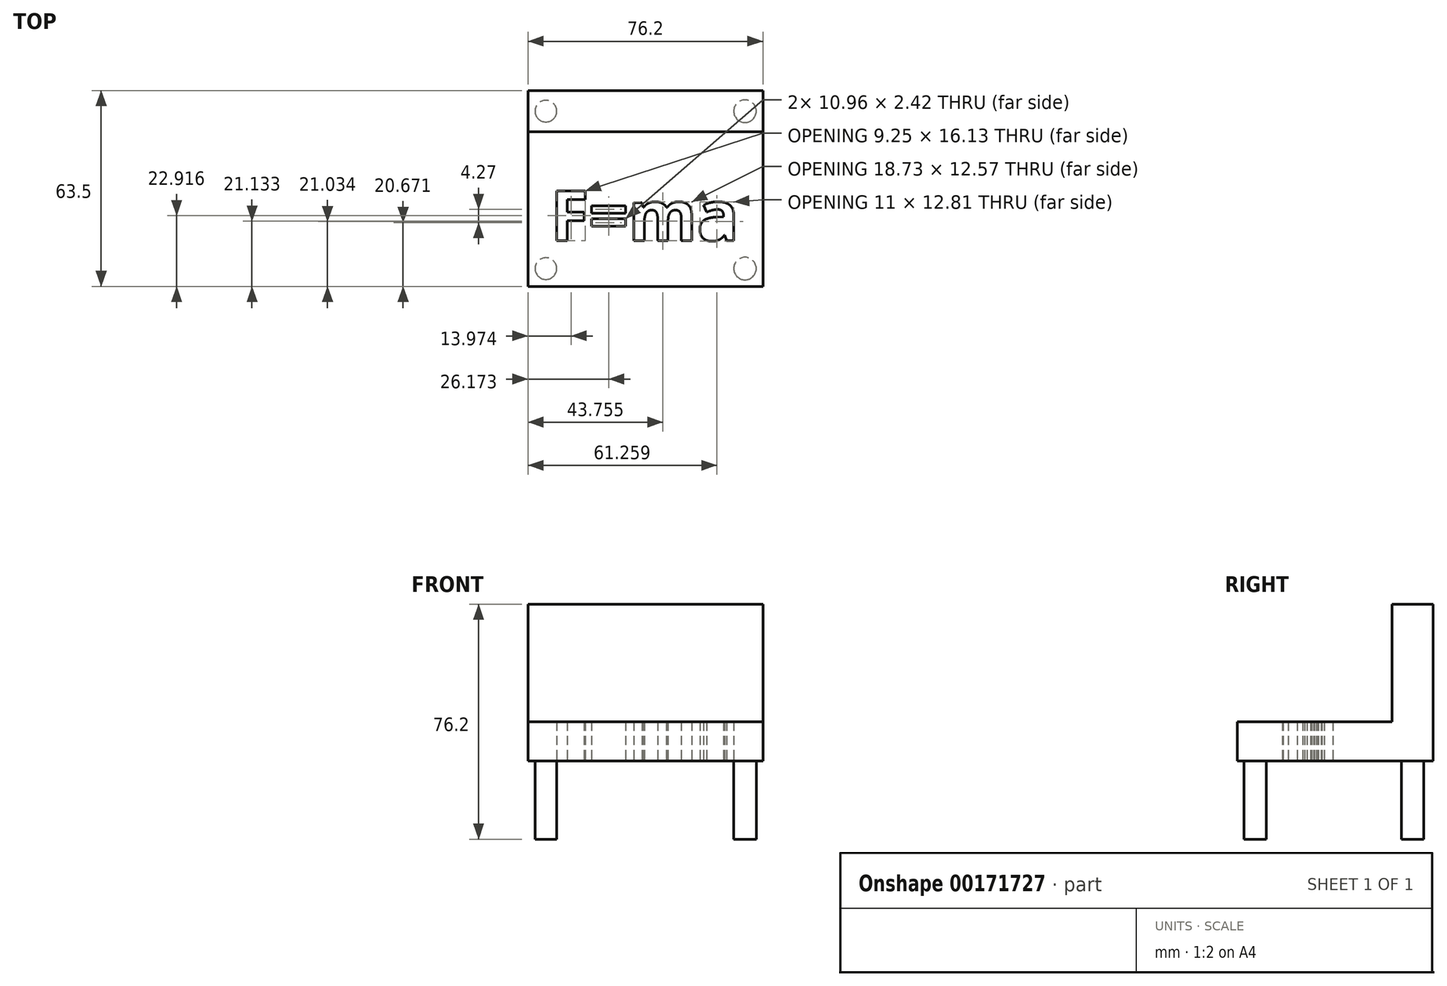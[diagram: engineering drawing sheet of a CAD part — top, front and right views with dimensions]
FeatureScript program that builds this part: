
annotation { "Feature Type Name" : "Feature", "Feature Type Description" : "" }
export const myFeature = defineFeature(function(context is Context, id is Id, definition is map)
    precondition{}
    {
        {
            var Q0;
            Q0=qCreatedBy(makeId("Top.planeOp"),FACE);
            var sketch = newSketch(context, id + "F0", { "sketchPlane" : qUnion([Q0])});
            skLineSegment(sketch, "E0.bottom", {"start": v(-23.67, 32.38) * mm, "end": v(52.53, 32.38) * mm});
            skLineSegment(sketch, "E0.top", {"start": v(-23.67, -31.12) * mm, "end": v(52.53, -31.12) * mm});
            skLineSegment(sketch, "E0.left", {"start": v(-23.67, 32.38) * mm, "end": v(-23.67, -31.12) * mm});
            skLineSegment(sketch, "E0.right", {"start": v(52.53, 32.38) * mm, "end": v(52.53, -31.12) * mm});
            skText(sketch, "E1", { "text": "F=ma", "fontName": "OpenSans-Bold.ttf"});
            const initialGuessF0  = {"E1": [-0.01635, -0.01627, 1, 0, 0.01627]};
            skSetInitialGuess(sketch, initialGuessF0);
            skSolve(sketch);
        }
        {
            var Q0;
            Q0 = qSketchRegion(id + "F0", true);
            extrude(context, id + "F1", {"entities" : qUnion([Q0]), "depth" : 12.7 * mm});
        }
        {
            var Q0;
            Q0=makeQuery(id+"F1.opExtrude","CAP_FACE",FACE,{"disambiguationData":[OSD([sQuery(id+"F0.wireOp",EDGE,"E0.bottom"),sQuery(id+"F0.wireOp",EDGE,"E0.top"),sQuery(id+"F0.wireOp",EDGE,"E0.left"),sQuery(id+"F0.wireOp",EDGE,"E0.right"),sQuery(id+"F0.wireOp",EDGE,"E1.sketch_text.stroke-0"),sQuery(id+"F0.wireOp",EDGE,"E1.sketch_text.stroke-1"),sQuery(id+"F0.wireOp",EDGE,"E1.sketch_text.stroke-2"),sQuery(id+"F0.wireOp",EDGE,"E1.sketch_text.stroke-3"),sQuery(id+"F0.wireOp",EDGE,"E1.sketch_text.stroke-4"),sQuery(id+"F0.wireOp",EDGE,"E1.sketch_text.stroke-5"),sQuery(id+"F0.wireOp",EDGE,"E1.sketch_text.stroke-6"),sQuery(id+"F0.wireOp",EDGE,"E1.sketch_text.stroke-7"),sQuery(id+"F0.wireOp",EDGE,"E1.sketch_text.stroke-8"),sQuery(id+"F0.wireOp",EDGE,"E1.sketch_text.stroke-9"),sQuery(id+"F0.wireOp",EDGE,"E1.sketch_text.stroke-10"),sQuery(id+"F0.wireOp",EDGE,"E1.sketch_text.stroke-11"),sQuery(id+"F0.wireOp",EDGE,"E1.sketch_text.stroke-12"),sQuery(id+"F0.wireOp",EDGE,"E1.sketch_text.stroke-13"),sQuery(id+"F0.wireOp",EDGE,"E1.sketch_text.stroke-14"),sQuery(id+"F0.wireOp",EDGE,"E1.sketch_text.stroke-15"),sQuery(id+"F0.wireOp",EDGE,"E1.sketch_text.stroke-16"),sQuery(id+"F0.wireOp",EDGE,"E1.sketch_text.stroke-17"),sQuery(id+"F0.wireOp",EDGE,"E1.sketch_text.stroke-18"),sQuery(id+"F0.wireOp",EDGE,"E1.sketch_text.stroke-19"),sQuery(id+"F0.wireOp",EDGE,"E1.sketch_text.stroke-20"),sQuery(id+"F0.wireOp",EDGE,"E1.sketch_text.stroke-21"),sQuery(id+"F0.wireOp",EDGE,"E1.sketch_text.stroke-22"),sQuery(id+"F0.wireOp",EDGE,"E1.sketch_text.stroke-23"),sQuery(id+"F0.wireOp",EDGE,"E1.sketch_text.stroke-24"),sQuery(id+"F0.wireOp",EDGE,"E1.sketch_text.stroke-25"),sQuery(id+"F0.wireOp",EDGE,"E1.sketch_text.stroke-26"),sQuery(id+"F0.wireOp",EDGE,"E1.sketch_text.stroke-27"),sQuery(id+"F0.wireOp",EDGE,"E1.sketch_text.stroke-28"),sQuery(id+"F0.wireOp",EDGE,"E1.sketch_text.stroke-29"),sQuery(id+"F0.wireOp",EDGE,"E1.sketch_text.stroke-30"),sQuery(id+"F0.wireOp",EDGE,"E1.sketch_text.stroke-31"),sQuery(id+"F0.wireOp",EDGE,"E1.sketch_text.stroke-32"),sQuery(id+"F0.wireOp",EDGE,"E1.sketch_text.stroke-33"),sQuery(id+"F0.wireOp",EDGE,"E1.sketch_text.stroke-34"),sQuery(id+"F0.wireOp",EDGE,"E1.sketch_text.stroke-35"),sQuery(id+"F0.wireOp",EDGE,"E1.sketch_text.stroke-36"),sQuery(id+"F0.wireOp",EDGE,"E1.sketch_text.stroke-37"),sQuery(id+"F0.wireOp",EDGE,"E1.sketch_text.stroke-38"),sQuery(id+"F0.wireOp",EDGE,"E1.sketch_text.stroke-39"),sQuery(id+"F0.wireOp",EDGE,"E1.sketch_text.stroke-40"),sQuery(id+"F0.wireOp",EDGE,"E1.sketch_text.stroke-41"),sQuery(id+"F0.wireOp",EDGE,"E1.sketch_text.stroke-42"),sQuery(id+"F0.wireOp",EDGE,"E1.sketch_text.stroke-43"),sQuery(id+"F0.wireOp",EDGE,"E1.sketch_text.stroke-44"),sQuery(id+"F0.wireOp",EDGE,"E1.sketch_text.stroke-45"),sQuery(id+"F0.wireOp",EDGE,"E1.sketch_text.stroke-46"),sQuery(id+"F0.wireOp",EDGE,"E1.sketch_text.stroke-47"),sQuery(id+"F0.wireOp",EDGE,"E1.sketch_text.stroke-48"),sQuery(id+"F0.wireOp",EDGE,"E1.sketch_text.stroke-49"),sQuery(id+"F0.wireOp",EDGE,"E1.sketch_text.stroke-50"),sQuery(id+"F0.wireOp",EDGE,"E1.sketch_text.stroke-51"),sQuery(id+"F0.wireOp",EDGE,"E1.sketch_text.stroke-52"),sQuery(id+"F0.wireOp",EDGE,"E1.sketch_text.stroke-53"),sQuery(id+"F0.wireOp",EDGE,"E1.sketch_text.stroke-54"),sQuery(id+"F0.wireOp",EDGE,"E1.sketch_text.stroke-55"),sQuery(id+"F0.wireOp",EDGE,"E1.sketch_text.stroke-56"),sQuery(id+"F0.wireOp",EDGE,"E1.sketch_text.stroke-57"),sQuery(id+"F0.wireOp",EDGE,"E1.sketch_text.stroke-58"),sQuery(id+"F0.wireOp",EDGE,"E1.sketch_text.stroke-59"),sQuery(id+"F0.wireOp",EDGE,"E1.sketch_text.stroke-60"),sQuery(id+"F0.wireOp",EDGE,"E1.sketch_text.stroke-61"),sQuery(id+"F0.wireOp",EDGE,"E1.sketch_text.stroke-62"),sQuery(id+"F0.wireOp",EDGE,"E1.sketch_text.stroke-63")])],"isStart":false});
            var sketch = newSketch(context, id + "F2", { "sketchPlane" : qUnion([Q0])});
            skLineSegment(sketch, "E2", {"start": v(-23.67, 18.99) * mm, "end": v(52.53, 18.99) * mm});
            skLineSegment(sketch, "E3", {"start": v(52.53, 18.99) * mm, "end": v(52.53, 32.38) * mm});
            skLineSegment(sketch, "E4", {"start": v(52.53, 32.38) * mm, "end": v(-23.67, 32.38) * mm});
            skLineSegment(sketch, "E5", {"start": v(-23.67, 32.38) * mm, "end": v(-23.67, 18.99) * mm});
            skSolve(sketch);
        }
        {
            var Q0;
            Q0 = qSketchRegion(id + "F2", true);
            extrude(context, id + "F3", {"entities" : qUnion([Q0]), "operationType" : NewBodyOperationType.ADD, "depth" : 38.1 * mm});
        }
        {
            var Q0;
            Q0=makeQuery(id+"F1.opExtrude","CAP_FACE",FACE,{"disambiguationData":[OSD([sQuery(id+"F0.wireOp",EDGE,"E0.bottom"),sQuery(id+"F0.wireOp",EDGE,"E0.top"),sQuery(id+"F0.wireOp",EDGE,"E0.left"),sQuery(id+"F0.wireOp",EDGE,"E0.right"),sQuery(id+"F0.wireOp",EDGE,"E1.sketch_text.stroke-0"),sQuery(id+"F0.wireOp",EDGE,"E1.sketch_text.stroke-1"),sQuery(id+"F0.wireOp",EDGE,"E1.sketch_text.stroke-2"),sQuery(id+"F0.wireOp",EDGE,"E1.sketch_text.stroke-3"),sQuery(id+"F0.wireOp",EDGE,"E1.sketch_text.stroke-4"),sQuery(id+"F0.wireOp",EDGE,"E1.sketch_text.stroke-5"),sQuery(id+"F0.wireOp",EDGE,"E1.sketch_text.stroke-6"),sQuery(id+"F0.wireOp",EDGE,"E1.sketch_text.stroke-7"),sQuery(id+"F0.wireOp",EDGE,"E1.sketch_text.stroke-8"),sQuery(id+"F0.wireOp",EDGE,"E1.sketch_text.stroke-9"),sQuery(id+"F0.wireOp",EDGE,"E1.sketch_text.stroke-10"),sQuery(id+"F0.wireOp",EDGE,"E1.sketch_text.stroke-11"),sQuery(id+"F0.wireOp",EDGE,"E1.sketch_text.stroke-12"),sQuery(id+"F0.wireOp",EDGE,"E1.sketch_text.stroke-13"),sQuery(id+"F0.wireOp",EDGE,"E1.sketch_text.stroke-14"),sQuery(id+"F0.wireOp",EDGE,"E1.sketch_text.stroke-15"),sQuery(id+"F0.wireOp",EDGE,"E1.sketch_text.stroke-16"),sQuery(id+"F0.wireOp",EDGE,"E1.sketch_text.stroke-17"),sQuery(id+"F0.wireOp",EDGE,"E1.sketch_text.stroke-18"),sQuery(id+"F0.wireOp",EDGE,"E1.sketch_text.stroke-19"),sQuery(id+"F0.wireOp",EDGE,"E1.sketch_text.stroke-20"),sQuery(id+"F0.wireOp",EDGE,"E1.sketch_text.stroke-21"),sQuery(id+"F0.wireOp",EDGE,"E1.sketch_text.stroke-22"),sQuery(id+"F0.wireOp",EDGE,"E1.sketch_text.stroke-23"),sQuery(id+"F0.wireOp",EDGE,"E1.sketch_text.stroke-24"),sQuery(id+"F0.wireOp",EDGE,"E1.sketch_text.stroke-25"),sQuery(id+"F0.wireOp",EDGE,"E1.sketch_text.stroke-26"),sQuery(id+"F0.wireOp",EDGE,"E1.sketch_text.stroke-27"),sQuery(id+"F0.wireOp",EDGE,"E1.sketch_text.stroke-28"),sQuery(id+"F0.wireOp",EDGE,"E1.sketch_text.stroke-29"),sQuery(id+"F0.wireOp",EDGE,"E1.sketch_text.stroke-30"),sQuery(id+"F0.wireOp",EDGE,"E1.sketch_text.stroke-31"),sQuery(id+"F0.wireOp",EDGE,"E1.sketch_text.stroke-32"),sQuery(id+"F0.wireOp",EDGE,"E1.sketch_text.stroke-33"),sQuery(id+"F0.wireOp",EDGE,"E1.sketch_text.stroke-34"),sQuery(id+"F0.wireOp",EDGE,"E1.sketch_text.stroke-35"),sQuery(id+"F0.wireOp",EDGE,"E1.sketch_text.stroke-36"),sQuery(id+"F0.wireOp",EDGE,"E1.sketch_text.stroke-37"),sQuery(id+"F0.wireOp",EDGE,"E1.sketch_text.stroke-38"),sQuery(id+"F0.wireOp",EDGE,"E1.sketch_text.stroke-39"),sQuery(id+"F0.wireOp",EDGE,"E1.sketch_text.stroke-40"),sQuery(id+"F0.wireOp",EDGE,"E1.sketch_text.stroke-41"),sQuery(id+"F0.wireOp",EDGE,"E1.sketch_text.stroke-42"),sQuery(id+"F0.wireOp",EDGE,"E1.sketch_text.stroke-43"),sQuery(id+"F0.wireOp",EDGE,"E1.sketch_text.stroke-44"),sQuery(id+"F0.wireOp",EDGE,"E1.sketch_text.stroke-45"),sQuery(id+"F0.wireOp",EDGE,"E1.sketch_text.stroke-46"),sQuery(id+"F0.wireOp",EDGE,"E1.sketch_text.stroke-47"),sQuery(id+"F0.wireOp",EDGE,"E1.sketch_text.stroke-48"),sQuery(id+"F0.wireOp",EDGE,"E1.sketch_text.stroke-49"),sQuery(id+"F0.wireOp",EDGE,"E1.sketch_text.stroke-50"),sQuery(id+"F0.wireOp",EDGE,"E1.sketch_text.stroke-51"),sQuery(id+"F0.wireOp",EDGE,"E1.sketch_text.stroke-52"),sQuery(id+"F0.wireOp",EDGE,"E1.sketch_text.stroke-53"),sQuery(id+"F0.wireOp",EDGE,"E1.sketch_text.stroke-54"),sQuery(id+"F0.wireOp",EDGE,"E1.sketch_text.stroke-55"),sQuery(id+"F0.wireOp",EDGE,"E1.sketch_text.stroke-56"),sQuery(id+"F0.wireOp",EDGE,"E1.sketch_text.stroke-57"),sQuery(id+"F0.wireOp",EDGE,"E1.sketch_text.stroke-58"),sQuery(id+"F0.wireOp",EDGE,"E1.sketch_text.stroke-59"),sQuery(id+"F0.wireOp",EDGE,"E1.sketch_text.stroke-60"),sQuery(id+"F0.wireOp",EDGE,"E1.sketch_text.stroke-61"),sQuery(id+"F0.wireOp",EDGE,"E1.sketch_text.stroke-62"),sQuery(id+"F0.wireOp",EDGE,"E1.sketch_text.stroke-63")])],"isStart":true});
            var sketch = newSketch(context, id + "F4", { "sketchPlane" : qUnion([Q0])});
            skCircle(sketch, "E6", {"center": v(46.73, -25.68) * mm, "radius": 3.66 * mm});
            skCircle(sketch, "E7", {"center": v(46.73, 25.35) * mm, "radius": 3.66 * mm});
            skCircle(sketch, "E8", {"center": v(-17.84, -25.68) * mm, "radius": 3.52 * mm});
            skCircle(sketch, "E9", {"center": v(-17.84, 25.35) * mm, "radius": 3.52 * mm});
            skSolve(sketch);
        }
        {
            var Q0;
            Q0 = qSketchRegion(id + "F4", true);
            extrude(context, id + "F5", {"entities" : qUnion([Q0]), "operationType" : NewBodyOperationType.ADD, "depth" : 25.4 * mm});
        }
    });
